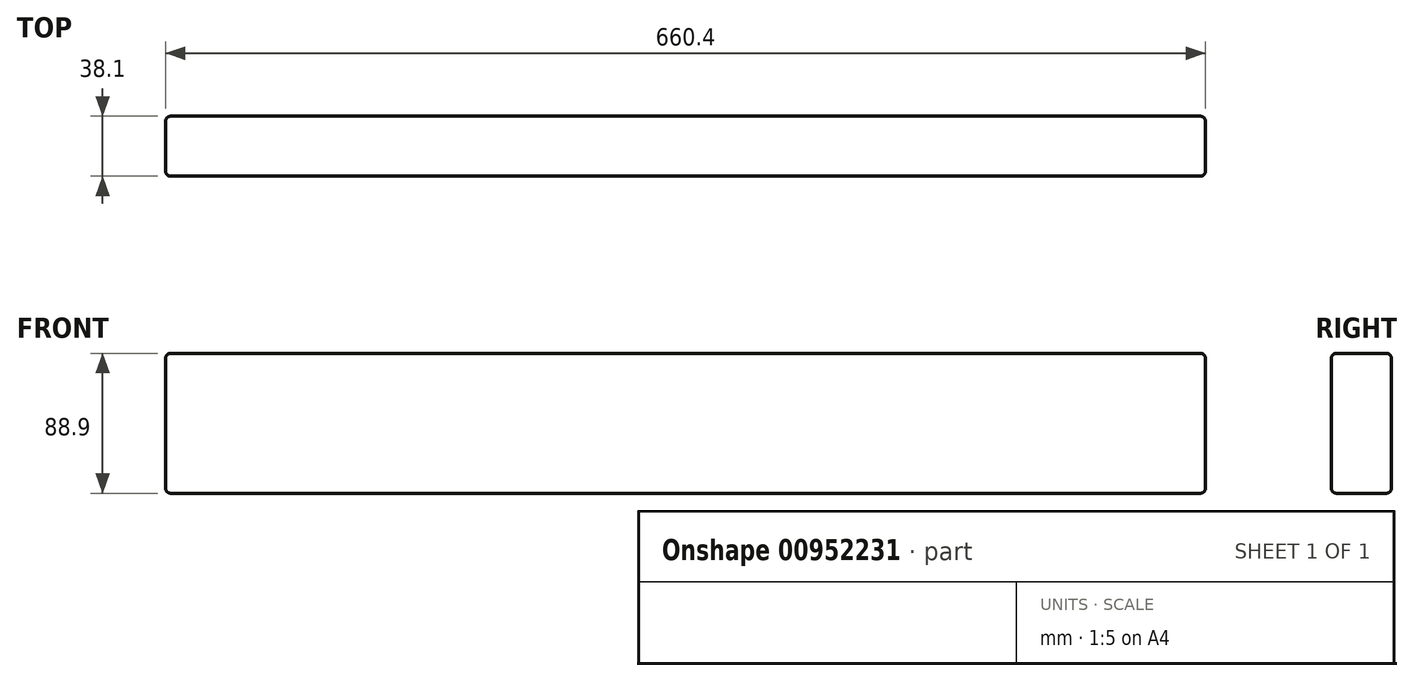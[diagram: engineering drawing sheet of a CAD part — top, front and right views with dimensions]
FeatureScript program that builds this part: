
annotation { "Feature Type Name" : "Feature", "Feature Type Description" : "" }
export const myFeature = defineFeature(function(context is Context, id is Id, definition is map)
    precondition{}
    {
        {
            var Q0;
            Q0=qCreatedBy(makeId("Front.planeOp"),FACE);
            var sketch = newSketch(context, id + "F0", { "sketchPlane" : qUnion([Q0])});
            skLineSegment(sketch, "E0.bottom", {"start": v(0, 0) * mm, "end": v(660.4, 0) * mm});
            skLineSegment(sketch, "E0.top", {"start": v(0, -88.9) * mm, "end": v(660.4, -88.9) * mm});
            skLineSegment(sketch, "E0.left", {"start": v(0, 0) * mm, "end": v(0, -88.9) * mm});
            skLineSegment(sketch, "E0.right", {"start": v(660.4, 0) * mm, "end": v(660.4, -88.9) * mm});
            skSolve(sketch);
        }
        {
            var Q0;
            Q0 = qSketchRegion(id + "F0", true);
            extrude(context, id + "F1", {"entities" : qUnion([Q0]), "depth" : 38.1 * mm, "offsetDistance" : 25.4 * mm});
        }
        {
            var Q0;
            Q0=makeQuery(id+"F1.opExtrude","CAP_EDGE",EDGE,{"disambiguationData":[OSD([sQuery(id+"F0.wireOp",EDGE,"E0.bottom")])],"isStart":false});
            var Q1;
            Q1=makeQuery(id+"F1.opExtrude","CAP_EDGE",EDGE,{"disambiguationData":[OSD([sQuery(id+"F0.wireOp",EDGE,"E0.bottom")])],"isStart":true});
            var Q2;
            Q2=makeQuery(id+"F1.opExtrude","SWEPT_EDGE",EDGE,{"disambiguationData":[OSD([sQuery(id+"F0.wireOp",EDGE,"E0.bottom"),sQuery(id+"F0.wireOp",EDGE,"E0.right")])]});
            var Q3;
            Q3=makeQuery(id+"F1.opExtrude","CAP_EDGE",EDGE,{"disambiguationData":[OSD([sQuery(id+"F0.wireOp",EDGE,"E0.right")])],"isStart":true});
            var Q4;
            Q4=makeQuery(id+"F1.opExtrude","CAP_EDGE",EDGE,{"disambiguationData":[OSD([sQuery(id+"F0.wireOp",EDGE,"E0.right")])],"isStart":false});
            var Q5;
            Q5=makeQuery(id+"F1.opExtrude","SWEPT_EDGE",EDGE,{"disambiguationData":[OSD([sQuery(id+"F0.wireOp",EDGE,"E0.top"),sQuery(id+"F0.wireOp",EDGE,"E0.right")])]});
            var Q6;
            Q6=makeQuery(id+"F1.opExtrude","CAP_EDGE",EDGE,{"disambiguationData":[OSD([sQuery(id+"F0.wireOp",EDGE,"E0.top")])],"isStart":false});
            var Q7;
            Q7=makeQuery(id+"F1.opExtrude","CAP_EDGE",EDGE,{"disambiguationData":[OSD([sQuery(id+"F0.wireOp",EDGE,"E0.top")])],"isStart":true});
            var Q8;
            Q8=makeQuery(id+"F1.opExtrude","CAP_EDGE",EDGE,{"disambiguationData":[OSD([sQuery(id+"F0.wireOp",EDGE,"E0.left")])],"isStart":true});
            var Q9;
            Q9=makeQuery(id+"F1.opExtrude","CAP_EDGE",EDGE,{"disambiguationData":[OSD([sQuery(id+"F0.wireOp",EDGE,"E0.left")])],"isStart":false});
            var Q10;
            Q10=makeQuery(id+"F1.opExtrude","SWEPT_EDGE",EDGE,{"disambiguationData":[OSD([sQuery(id+"F0.wireOp",EDGE,"E0.top"),sQuery(id+"F0.wireOp",EDGE,"E0.left")])]});
            var Q11;
            Q11=makeQuery(id+"F1.opExtrude","SWEPT_EDGE",EDGE,{"disambiguationData":[OSD([sQuery(id+"F0.wireOp",EDGE,"E0.bottom"),sQuery(id+"F0.wireOp",EDGE,"E0.left")])]});
            fillet(context, id + "F2", {"entities" : qUnion([Q0, Q1, Q2, Q3, Q4, Q5, Q6, Q7, Q8, Q9, Q10, Q11]), "radius" : 3.17 * mm, "tangentPropagation" : true, "allowEdgeOverflow" : false});
        }
    });
